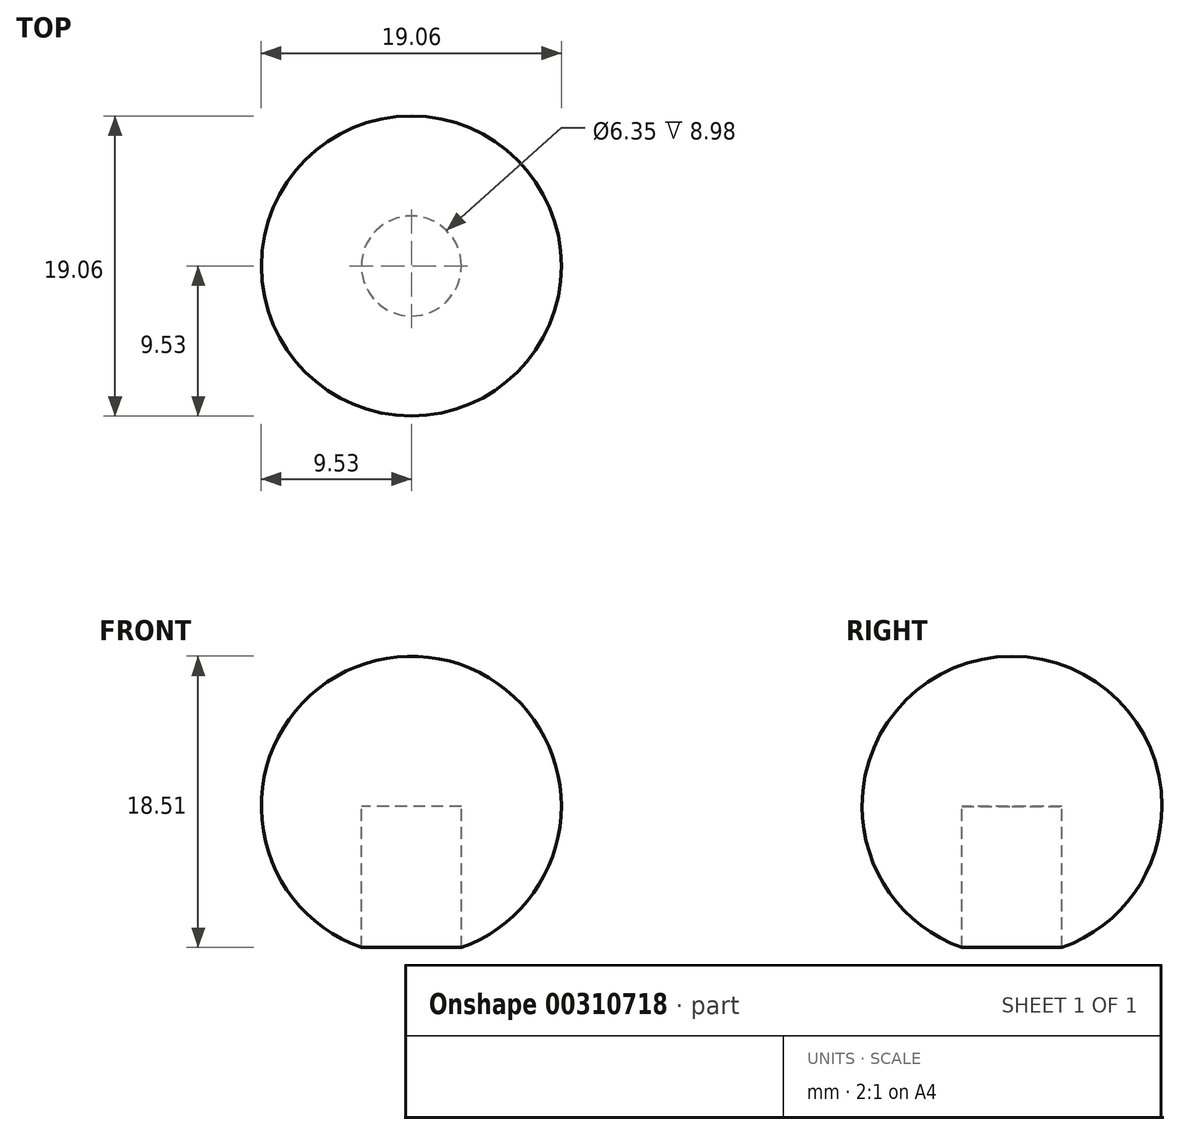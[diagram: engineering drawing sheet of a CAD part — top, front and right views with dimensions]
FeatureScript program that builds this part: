
annotation { "Feature Type Name" : "Feature", "Feature Type Description" : "" }
export const myFeature = defineFeature(function(context is Context, id is Id, definition is map)
    precondition{}
    {
        {
            var Q0;
            Q0=qCreatedBy(makeId("Top.planeOp"),FACE);
            var sketch = newSketch(context, id + "F0", { "sketchPlane" : qUnion([Q0])});
            skArc(sketch, "E0", {"start": v(0, 9.53) * mm, "mid": v(-9.53, 0) * mm, "end": v(0, -9.53) * mm});
            skLineSegment(sketch, "E1", {"start": v(0, 9.53) * mm, "end": v(0, -9.53) * mm});
            skSolve(sketch);
        }
        {
            var Q0;
            Q0=qCreatedBy(makeId("Front.planeOp"),FACE);
            var sketch = newSketch(context, id + "F1", { "sketchPlane" : qUnion([Q0])});
            skCircle(sketch, "E2", {"center": v(0, 0) * mm, "radius": 9.53 * mm});
            skSolve(sketch);
        }
        {
            var Q0;
            Q0=makeQuery(id+"F0.imprint","IMPRINT",FACE,{"disambiguationData":[TD([[makeQuery(id+"F0.imprint","IMPRINT",EDGE,{"derivedFrom":sQuery(id+"F0.wireOp",EDGE,"E0")}),1.0]])]});
            var Q1;
            Q1=sQuery(id+"F1.wireOp",EDGE,"E2");
            revolve(context, id + "F2", {"entities" : qUnion([Q0]), "axis" : qUnion([Q1]), "revolveType" : RevolveType.FULL});
        }
        {
            var Q0;
            Q0=qCreatedBy(makeId("Top.planeOp"),FACE);
            var sketch = newSketch(context, id + "F3", { "sketchPlane" : qUnion([Q0])});
            skCircle(sketch, "E3", {"center": v(0, 0) * mm, "radius": 3.18 * mm});
            skSolve(sketch);
        }
        {
            var Q0;
            Q0=makeQuery(id+"F3.imprint","IMPRINT",FACE,{"disambiguationData":[TD([[makeQuery(id+"F3.imprint","IMPRINT",EDGE,{"derivedFrom":sQuery(id+"F3.wireOp",EDGE,"E3")}),1.0]])]});
            var Q1;
            Q1=sQuery(id+"F3.wireOp",EDGE,"E3");
            extrude(context, id + "F4", {"entities" : qUnion([Q0]), "surfaceEntities" : qUnion([Q1]), "oppositeDirection" : true, "depth" : 50.8 * mm});
        }
        {
            var Q0;
            Q0=makeQuery(id+"F4.opExtrude","SWEPT_BODY",BODY,{"disambiguationData":[OSD([sQuery(id+"F3.wireOp",EDGE,"E3")])]});
            var Q1;
            Q1=makeQuery(id+"F2.opRevolve","SWEPT_BODY",BODY,{"disambiguationData":[OSD([sQuery(id+"F0.wireOp",EDGE,"E0"),sQuery(id+"F0.wireOp",EDGE,"E1")])]});
            booleanBodies(context, id + "F5", {"operationType" : BooleanOperationType.SUBTRACTION, "tools" : qUnion([Q0]), "targets" : qUnion([Q1])});
        }
    });
